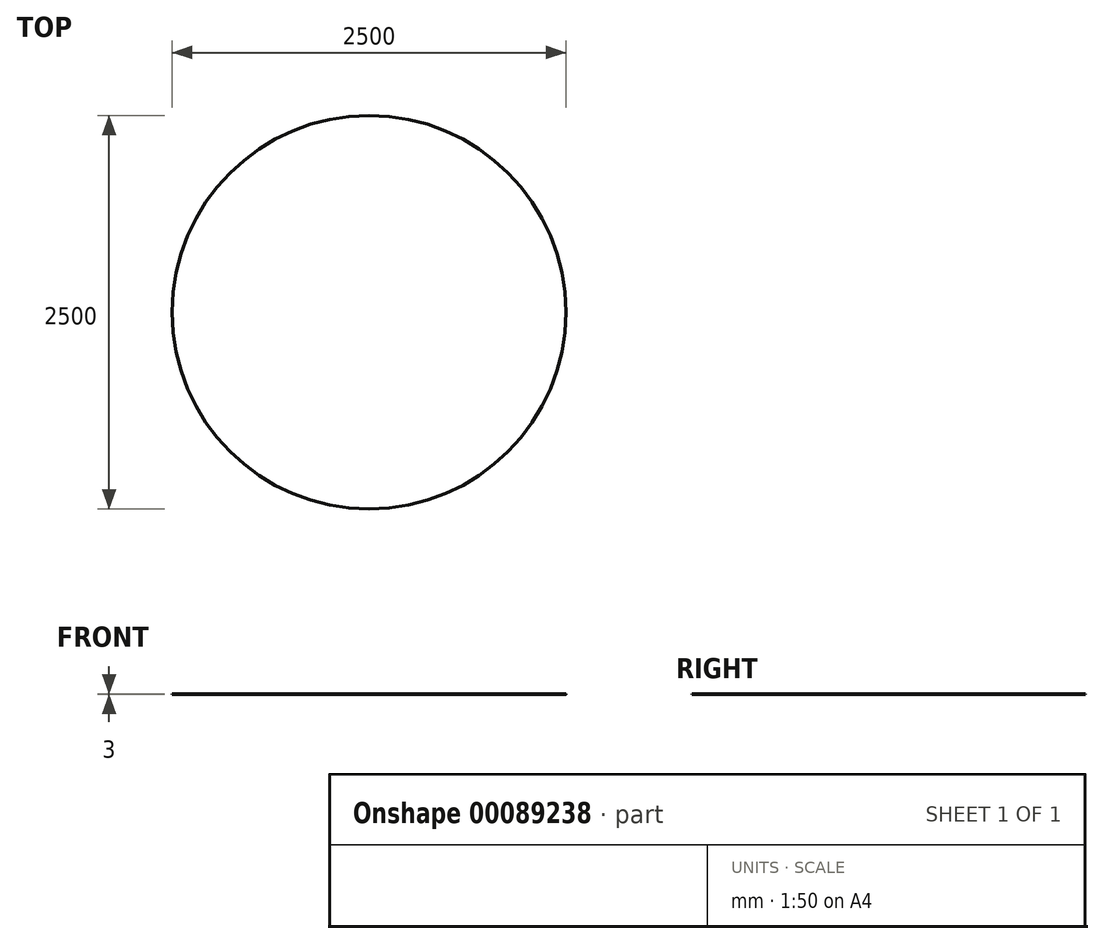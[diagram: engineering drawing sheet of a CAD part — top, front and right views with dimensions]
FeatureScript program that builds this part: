
annotation { "Feature Type Name" : "Feature", "Feature Type Description" : "" }
export const myFeature = defineFeature(function(context is Context, id is Id, definition is map)
    precondition{}
    {
        {
            var Q0;
            Q0=qCreatedBy(makeId("Top.planeOp"),FACE);
            var sketch = newSketch(context, id + "F0", { "sketchPlane" : qUnion([Q0])});
            skCircle(sketch, "E0", {"center": v(0, 0) * mm, "radius": 1250 * mm});
            skLineSegment(sketch, "E1", {"start": v(0, 1250) * mm, "end": v(0, -1250) * mm});
            skSolve(sketch);
        }
        {
            var Q0;
            {var subQ0=sQuery(id+"F0.wireOp",EDGE,"E1");Q0=makeQuery(id+"F0.imprint","IMPRINT",FACE,{"disambiguationData":[TD([[makeQuery(id+"F0.imprint","IMPRINT",EDGE,{"derivedFrom":subQ0}),-1.0]])]});}
            var Q1;
            {var subQ0=sQuery(id+"F0.wireOp",EDGE,"E1");Q1=makeQuery(id+"F0.imprint","IMPRINT",FACE,{"disambiguationData":[TD([[makeQuery(id+"F0.imprint","IMPRINT",EDGE,{"derivedFrom":subQ0}),1.0]])]});}
            extrude(context, id + "F1", {"entities" : qUnion([Q0, Q1]), "depth" : 3 * mm});
        }
    });
